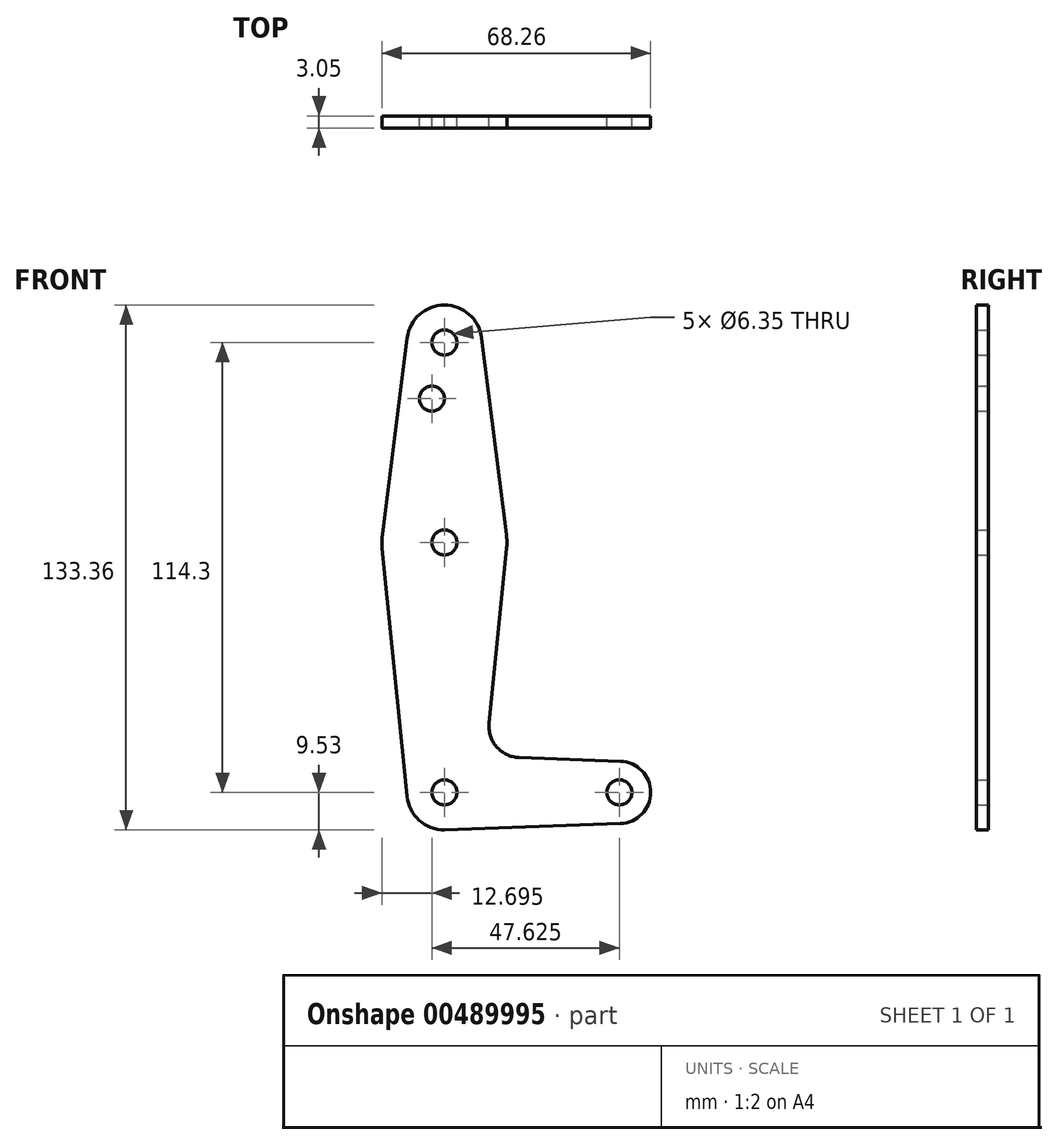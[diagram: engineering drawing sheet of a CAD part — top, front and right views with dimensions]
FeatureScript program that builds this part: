
annotation { "Feature Type Name" : "Feature", "Feature Type Description" : "" }
export const myFeature = defineFeature(function(context is Context, id is Id, definition is map)
    precondition{}
    {
        {
            var Q0;
            Q0=qCreatedBy(makeId("Front.planeOp"),FACE);
            var sketch = newSketch(context, id + "F0", { "sketchPlane" : qUnion([Q0])});
            skLineSegment(sketch, "E0", {"start": v(0, 0) * mm, "end": v(0, 114.3) * mm});
            skLineSegment(sketch, "E1", {"start": v(0, 0) * mm, "end": v(44.45, 0) * mm});
            skCircle(sketch, "E2", {"center": v(0, 114.3) * mm, "radius": 9.53 * mm});
            skCircle(sketch, "E3", {"center": v(0, 63.5) * mm, "radius": 15.88 * mm});
            skCircle(sketch, "E4", {"center": v(0, 0) * mm, "radius": 9.53 * mm});
            skCircle(sketch, "E5", {"center": v(44.45, 0) * mm, "radius": 7.94 * mm});
            skLineSegment(sketch, "E6", {"start": v(-9.45, 115.5) * mm, "end": v(-15.75, 65.48) * mm});
            skLineSegment(sketch, "E7", {"start": v(9.45, 115.5) * mm, "end": v(15.75, 65.48) * mm});
            skLineSegment(sketch, "E8", {"start": v(15.8, 61.91) * mm, "end": v(11.34, 17.6) * mm});
            skLineSegment(sketch, "E9", {"start": v(0, -9.53) * mm, "end": v(44.73, -7.93) * mm});
            skCircle(sketch, "E10", {"center": v(0, 114.3) * mm, "radius": 3.18 * mm});
            skCircle(sketch, "E11", {"center": v(0, 63.5) * mm, "radius": 3.18 * mm});
            skCircle(sketch, "E12", {"center": v(44.45, 0) * mm, "radius": 3.18 * mm});
            skCircle(sketch, "E13", {"center": v(0, 0) * mm, "radius": 3.18 * mm});
            skLineSegment(sketch, "E14", {"start": v(-15.8, 61.91) * mm, "end": v(-9.48, -0.95) * mm});
            skLineSegment(sketch, "E15", {"start": v(18.97, 8.85) * mm, "end": v(44.73, 7.93) * mm});
            skArc(sketch, "E16.filletArc", {"start": v(11.34, 17.6) * mm, "mid": v(13.26, 11.57) * mm, "end": v(18.97, 8.85) * mm});
            skCircle(sketch, "E17", {"center": v(-3.18, 100.03) * mm, "radius": 3.18 * mm});
            skSolve(sketch);
        }
        {
            var Q0;
            {var subQ0=sQuery(id+"F0.wireOp",EDGE,"E8");Q0=makeQuery(id+"F0.imprint","IMPRINT",FACE,{"disambiguationData":[TD([[makeQuery(id+"F0.imprint","IMPRINT",EDGE,{"derivedFrom":subQ0}),-1.0]])]});}
            var Q1;
            {var subQ0=sQuery(id+"F0.wireOp",EDGE,"E3");var subQ3=sQuery(id+"F0.wireOp",EDGE,"E0");var subQ7=makeQuery(id+"F0.imprint","INTERSECT",VERTEX,{"disambiguationData":[OD(0.0)],"derivedFrom":[subQ3,subQ0]});Q1=makeQuery(id+"F0.imprint","IMPRINT",FACE,{"disambiguationData":[TD([[makeQuery(id+"F0.imprint","IMPRINT",EDGE,{"disambiguationData":[TD([[subQ7,-1.0]])],"derivedFrom":subQ3}),1.0]])]});}
            var Q2;
            {var subQ4=sQuery(id+"F0.wireOp",EDGE,"E13");var subQ5=sQuery(id+"F0.wireOp",EDGE,"E0");var subQ6=makeQuery(id+"F0.imprint","INTERSECT",VERTEX,{"derivedFrom":[subQ5,subQ4]});Q2=makeQuery(id+"F0.imprint","IMPRINT",FACE,{"disambiguationData":[TD([[makeQuery(id+"F0.imprint","IMPRINT",EDGE,{"disambiguationData":[TD([[subQ6,-1.0]])],"derivedFrom":subQ5}),1.0]])]});}
            var Q3;
            Q3=makeQuery(id+"F0.imprint","IMPRINT",FACE,{"disambiguationData":[TD([[makeQuery(id+"F0.imprint","IMPRINT",EDGE,{"derivedFrom":sQuery(id+"F0.wireOp",EDGE,"E12")}),-1.0]])]});
            var Q4;
            {var subQ0=sQuery(id+"F0.wireOp",EDGE,"E7");Q4=makeQuery(id+"F0.imprint","IMPRINT",FACE,{"disambiguationData":[TD([[makeQuery(id+"F0.imprint","IMPRINT",EDGE,{"derivedFrom":subQ0}),-1.0]])]});}
            var Q5;
            {var subQ0=sQuery(id+"F0.wireOp",EDGE,"E3");var subQ2=sQuery(id+"F0.wireOp",EDGE,"E0");var subQ3=makeQuery(id+"F0.imprint","INTERSECT",VERTEX,{"disambiguationData":[OD(0.0)],"derivedFrom":[subQ2,subQ0]});Q5=makeQuery(id+"F0.imprint","IMPRINT",FACE,{"disambiguationData":[TD([[makeQuery(id+"F0.imprint","IMPRINT",EDGE,{"disambiguationData":[TD([[subQ3,-1.0]])],"derivedFrom":subQ2}),-1.0]])]});}
            var Q6;
            {var subQ0=sQuery(id+"F0.wireOp",EDGE,"E6");Q6=makeQuery(id+"F0.imprint","IMPRINT",FACE,{"disambiguationData":[TD([[makeQuery(id+"F0.imprint","IMPRINT",EDGE,{"derivedFrom":subQ0}),1.0]])]});}
            var Q7;
            {var subQ0=sQuery(id+"F0.wireOp",EDGE,"05S5LIzZ-ywF0-MxzV-lBV3-b6y1glVUUf3L");var subQ1=sQuery(id+"F0.wireOp",EDGE,"E0");var subQ2=makeQuery(id+"F0.imprint","INTERSECT",VERTEX,{"disambiguationData":[OD(0.0)],"derivedFrom":[subQ1,subQ0]});Q7=makeQuery(id+"F0.imprint","IMPRINT",FACE,{"disambiguationData":[TD([[makeQuery(id+"F0.imprint","IMPRINT",EDGE,{"disambiguationData":[TD([[subQ2,-1.0]])],"derivedFrom":subQ1}),1.0]])]});}
            var Q8;
            {var subQ0=sQuery(id+"F0.wireOp",EDGE,"05S5LIzZ-ywF0-MxzV-lBV3-b6y1glVUUf3L");var subQ1=sQuery(id+"F0.wireOp",EDGE,"E0");var subQ2=makeQuery(id+"F0.imprint","INTERSECT",VERTEX,{"disambiguationData":[OD(0.0)],"derivedFrom":[subQ1,subQ0]});Q8=makeQuery(id+"F0.imprint","IMPRINT",FACE,{"disambiguationData":[TD([[makeQuery(id+"F0.imprint","IMPRINT",EDGE,{"disambiguationData":[TD([[subQ2,-1.0]])],"derivedFrom":subQ1}),-1.0]])]});}
            var Q9;
            {var subQ0=sQuery(id+"F0.wireOp",EDGE,"E13");var subQ1=sQuery(id+"F0.wireOp",EDGE,"E0");var subQ2=makeQuery(id+"F0.imprint","INTERSECT",VERTEX,{"derivedFrom":[subQ1,subQ0]});Q9=makeQuery(id+"F0.imprint","IMPRINT",FACE,{"disambiguationData":[TD([[makeQuery(id+"F0.imprint","IMPRINT",EDGE,{"disambiguationData":[TD([[subQ2,-1.0]])],"derivedFrom":subQ1}),-1.0]])]});}
            var Q10;
            {var subQ5=sQuery(id+"F0.wireOp",EDGE,"E14");Q10=makeQuery(id+"F0.imprint","IMPRINT",FACE,{"disambiguationData":[TD([[makeQuery(id+"F0.imprint","IMPRINT",EDGE,{"derivedFrom":subQ5}),1.0]])]});}
            var Q11;
            {var subQ0=sQuery(id+"F0.wireOp",EDGE,"E5");var subQ1=sQuery(id+"F0.wireOp",EDGE,"E1");var subQ2=makeQuery(id+"F0.imprint","INTERSECT",VERTEX,{"derivedFrom":[subQ1,subQ0]});Q11=makeQuery(id+"F0.imprint","IMPRINT",FACE,{"disambiguationData":[TD([[makeQuery(id+"F0.imprint","IMPRINT",EDGE,{"disambiguationData":[TD([[subQ2,1.0]])],"derivedFrom":subQ1}),-1.0]])]});}
            var Q12;
            Q12=makeQuery(id+"F0.imprint","IMPRINT",FACE,{"disambiguationData":[TD([[makeQuery(id+"F0.imprint","IMPRINT",EDGE,{"derivedFrom":sQuery(id+"F0.wireOp",EDGE,"E10")}),-1.0]])]});
            var Q13;
            {var subQ0=sQuery(id+"F0.wireOp",EDGE,"E9");var subQ1=sQuery(id+"F0.wireOp",EDGE,"E4");var subQ2=makeQuery(id+"F0.imprint","INTERSECT",VERTEX,{"disambiguationData":[OD(0.0)],"derivedFrom":[subQ1,subQ0]});Q13=makeQuery(id+"F0.imprint","IMPRINT",FACE,{"disambiguationData":[TD([[makeQuery(id+"F0.imprint","IMPRINT",EDGE,{"disambiguationData":[TD([[subQ2,-1.0]])],"derivedFrom":subQ1}),1.0]])]});}
            extrude(context, id + "F1", {"entities" : qUnion([Q0, Q1, Q2, Q3, Q4, Q5, Q6, Q7, Q8, Q9, Q10, Q11, Q12, Q13]), "depth" : 3.05 * mm});
        }
    });
